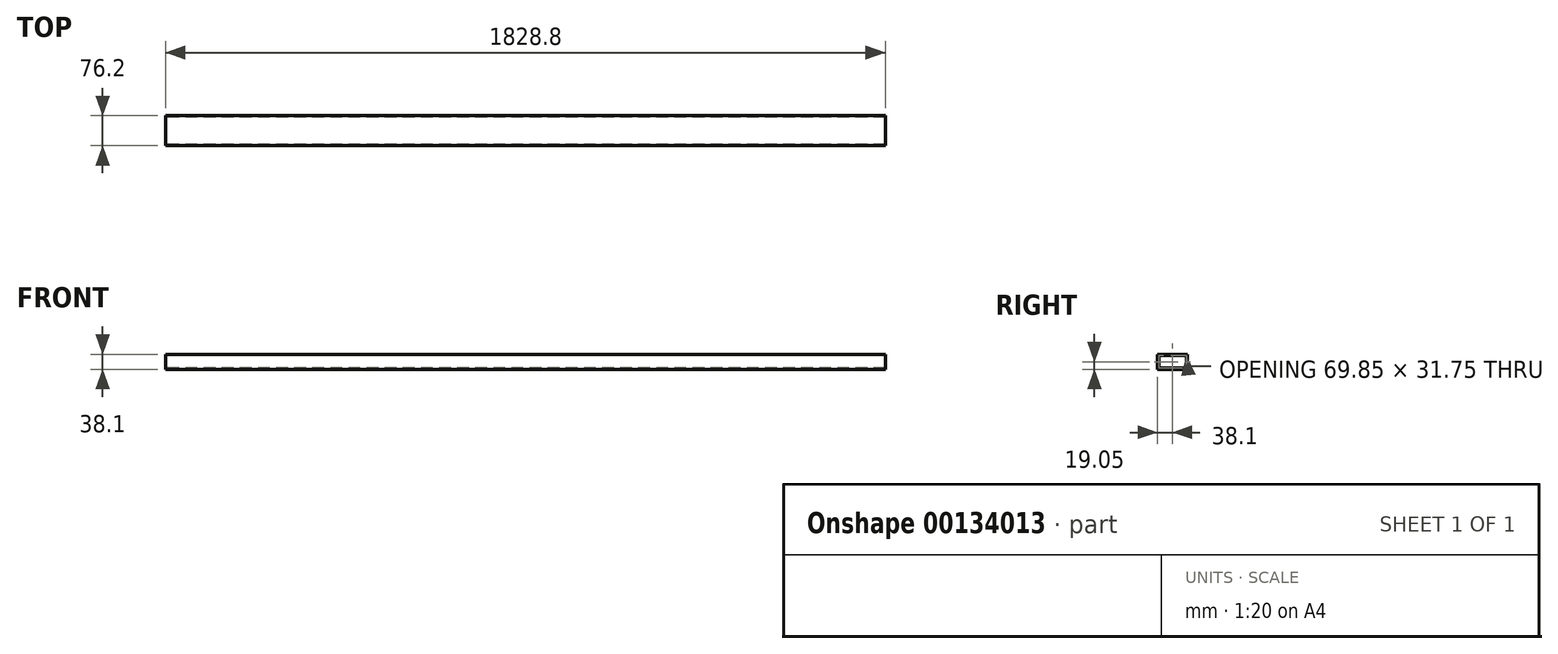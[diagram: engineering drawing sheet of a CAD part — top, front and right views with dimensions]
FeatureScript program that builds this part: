
annotation { "Feature Type Name" : "Feature", "Feature Type Description" : "" }
export const myFeature = defineFeature(function(context is Context, id is Id, definition is map)
    precondition{}
    {
        {
            var Q0;
            Q0=qCreatedBy(makeId("Right.planeOp"),FACE);
            var sketch = newSketch(context, id + "F0", { "sketchPlane" : qUnion([Q0])});
            skLineSegment(sketch, "E0.bottom", {"start": v(-38.1, 19.05) * mm, "end": v(38.1, 19.05) * mm});
            skLineSegment(sketch, "E0.top", {"start": v(-38.1, -19.05) * mm, "end": v(38.1, -19.05) * mm});
            skLineSegment(sketch, "E0.left", {"start": v(-38.1, 19.05) * mm, "end": v(-38.1, -19.05) * mm});
            skLineSegment(sketch, "E0.right", {"start": v(38.1, 19.05) * mm, "end": v(38.1, -19.05) * mm});
            skLineSegment(sketch, "E1", {"start": v(0, 19.05) * mm, "end": v(0, -19.05) * mm, "construction": true});
            skLineSegment(sketch, "E2.0", {"start": v(-33.4, 15.87) * mm, "end": v(33.4, 15.87) * mm});
            skLineSegment(sketch, "E2.1", {"start": v(-34.92, 14.35) * mm, "end": v(-34.92, -14.35) * mm});
            skLineSegment(sketch, "E2.2", {"start": v(-33.4, -15.87) * mm, "end": v(33.4, -15.87) * mm});
            skLineSegment(sketch, "E2.3", {"start": v(34.92, 14.35) * mm, "end": v(34.92, -14.35) * mm});
            skPoint(sketch, "E3.visualSharp", {"position": v(-34.93, 15.87) * mm});
            skArc(sketch, "E3.filletArc", {"start": v(-33.4, 15.87) * mm, "mid": v(-34.48, 15.43) * mm, "end": v(-34.92, 14.35) * mm});
            skPoint(sketch, "E4.visualSharp", {"position": v(-34.92, -15.87) * mm});
            skArc(sketch, "E4.filletArc", {"start": v(-34.93, -14.35) * mm, "mid": v(-34.48, -15.43) * mm, "end": v(-33.4, -15.88) * mm});
            skPoint(sketch, "E5.visualSharp", {"position": v(34.93, 15.87) * mm});
            skArc(sketch, "E5.filletArc", {"start": v(34.93, 14.35) * mm, "mid": v(34.48, 15.43) * mm, "end": v(33.4, 15.88) * mm});
            skPoint(sketch, "E6.visualSharp", {"position": v(34.93, -15.87) * mm});
            skArc(sketch, "E6.filletArc", {"start": v(33.4, -15.87) * mm, "mid": v(34.48, -15.43) * mm, "end": v(34.93, -14.35) * mm});
            skSolve(sketch);
        }
        {
            var Q0;
            Q0 = qSketchRegion(id + "F0", true);
            extrude(context, id + "F1", {"entities" : qUnion([Q0]), "endBound" : BoundingType.SYMMETRIC, "depth" : 1828.8 * mm});
        }
    });
